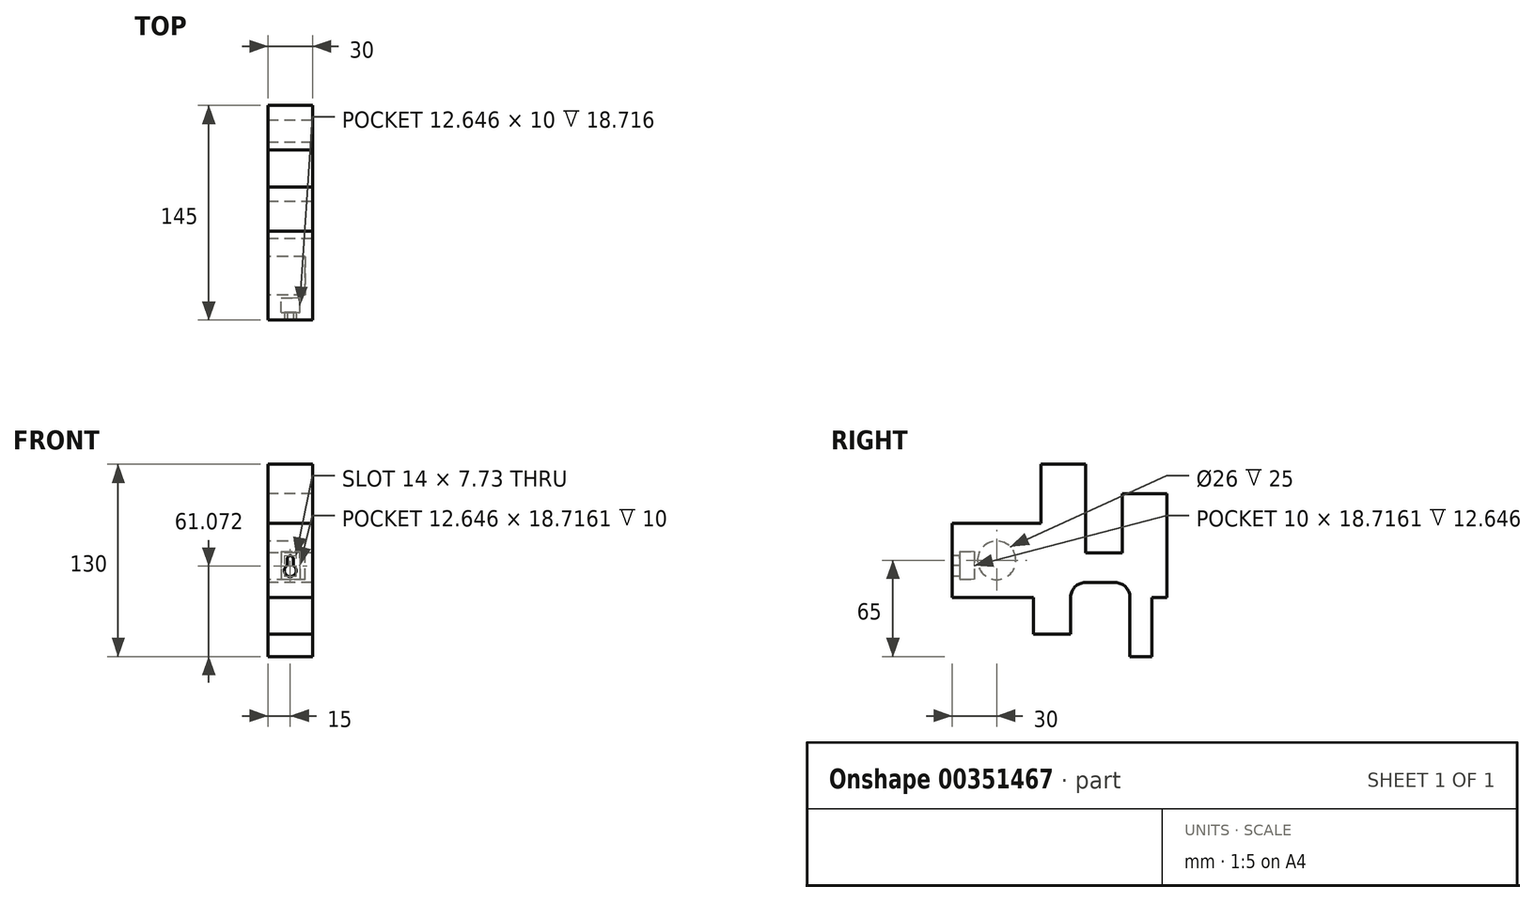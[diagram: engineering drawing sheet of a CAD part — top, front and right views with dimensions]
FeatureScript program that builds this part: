
annotation { "Feature Type Name" : "Feature", "Feature Type Description" : "" }
export const myFeature = defineFeature(function(context is Context, id is Id, definition is map)
    precondition{}
    {
        {
            var Q0;
            Q0=qCreatedBy(makeId("Right.planeOp"),FACE);
            var sketch = newSketch(context, id + "F0", { "sketchPlane" : qUnion([Q0])});
            skLineSegment(sketch, "E0", {"start": v(0, 0) * mm, "end": v(55, 0) * mm});
            skLineSegment(sketch, "E1", {"start": v(55, 0) * mm, "end": v(55, -25) * mm});
            skLineSegment(sketch, "E2", {"start": v(55, -25) * mm, "end": v(80, -25) * mm});
            skLineSegment(sketch, "E3", {"start": v(80, -25) * mm, "end": v(80, 0) * mm});
            skLineSegment(sketch, "E4", {"start": v(90, 10) * mm, "end": v(110, 10) * mm});
            skLineSegment(sketch, "E5", {"start": v(120, 0) * mm, "end": v(120, -40) * mm});
            skLineSegment(sketch, "E6", {"start": v(120, -40) * mm, "end": v(135, -40) * mm});
            skLineSegment(sketch, "E7", {"start": v(135, -40) * mm, "end": v(135, 0) * mm});
            skLineSegment(sketch, "E8", {"start": v(135, 0) * mm, "end": v(145, 0) * mm});
            skLineSegment(sketch, "E9", {"start": v(145, 0) * mm, "end": v(145, 70) * mm});
            skLineSegment(sketch, "E10", {"start": v(145, 70) * mm, "end": v(115, 70) * mm});
            skLineSegment(sketch, "E11", {"start": v(115, 70) * mm, "end": v(115, 30) * mm});
            skLineSegment(sketch, "E12", {"start": v(115, 30) * mm, "end": v(90, 30) * mm});
            skLineSegment(sketch, "E13", {"start": v(90, 30) * mm, "end": v(90, 90) * mm});
            skLineSegment(sketch, "E14", {"start": v(90, 90) * mm, "end": v(60, 90) * mm});
            skLineSegment(sketch, "E15", {"start": v(60, 90) * mm, "end": v(60, 50) * mm});
            skLineSegment(sketch, "E16", {"start": v(60, 50) * mm, "end": v(0, 50) * mm});
            skLineSegment(sketch, "E17", {"start": v(0, 50) * mm, "end": v(0, 0) * mm});
            skPoint(sketch, "E18.visualSharp", {"position": v(80, 10) * mm});
            skArc(sketch, "E18.filletArc", {"start": v(90, 10) * mm, "mid": v(82.93, 7.07) * mm, "end": v(80, 0) * mm});
            skPoint(sketch, "E19.visualSharp", {"position": v(120, 10) * mm});
            skArc(sketch, "E19.filletArc", {"start": v(120, 0) * mm, "mid": v(117.07, 7.07) * mm, "end": v(110, 10) * mm});
            skCircle(sketch, "E20", {"center": v(30, 25) * mm, "radius": 13 * mm});
            skSolve(sketch);
        }
        {
            var Q0;
            Q0=makeQuery(id+"F0.imprint","IMPRINT",FACE,{"disambiguationData":[TD([[makeQuery(id+"F0.imprint","IMPRINT",EDGE,{"derivedFrom":sQuery(id+"F0.wireOp",EDGE,"E0")}),1.0]])]});
            extrude(context, id + "F1", {"entities" : qUnion([Q0]), "depth" : 30 * mm});
        }
        {
            var Q0;
            Q0=makeQuery(id+"F1.opExtrude","CAP_FACE",FACE,{"disambiguationData":[OSD([sQuery(id+"F0.wireOp",EDGE,"E0"),sQuery(id+"F0.wireOp",EDGE,"E1"),sQuery(id+"F0.wireOp",EDGE,"E2"),sQuery(id+"F0.wireOp",EDGE,"E3"),sQuery(id+"F0.wireOp",EDGE,"E4"),sQuery(id+"F0.wireOp",EDGE,"E5"),sQuery(id+"F0.wireOp",EDGE,"E6"),sQuery(id+"F0.wireOp",EDGE,"E7"),sQuery(id+"F0.wireOp",EDGE,"E8"),sQuery(id+"F0.wireOp",EDGE,"E9"),sQuery(id+"F0.wireOp",EDGE,"E10"),sQuery(id+"F0.wireOp",EDGE,"E11"),sQuery(id+"F0.wireOp",EDGE,"E12"),sQuery(id+"F0.wireOp",EDGE,"E13"),sQuery(id+"F0.wireOp",EDGE,"E14"),sQuery(id+"F0.wireOp",EDGE,"E15"),sQuery(id+"F0.wireOp",EDGE,"E16"),sQuery(id+"F0.wireOp",EDGE,"E17"),sQuery(id+"F0.wireOp",EDGE,"E18.filletArc"),sQuery(id+"F0.wireOp",EDGE,"E19.filletArc"),sQuery(id+"F0.wireOp",EDGE,"E20")])],"isStart":false});
            var sketch = newSketch(context, id + "F2", { "sketchPlane" : qUnion([Q0])});
            skLineSegment(sketch, "E21.bottom", {"start": v(0, 50) * mm, "end": v(55, 50) * mm});
            skLineSegment(sketch, "E21.top", {"start": v(0, 0) * mm, "end": v(55, 0) * mm});
            skLineSegment(sketch, "E21.left", {"start": v(0, 50) * mm, "end": v(0, 0) * mm});
            skLineSegment(sketch, "E21.right", {"start": v(55, 50) * mm, "end": v(55, 0) * mm});
            skSolve(sketch);
        }
        {
            var Q0;
            Q0 = qSketchRegion(id + "F2", true);
            extrude(context, id + "F3", {"entities" : qUnion([Q0]), "operationType" : NewBodyOperationType.ADD, "oppositeDirection" : true, "depth" : 5 * mm});
        }
        {
            var Q0;
            Q0=makeQuery(id+"F1.opExtrude","SWEPT_FACE",FACE,{"disambiguationData":[OSD([sQuery(id+"F0.wireOp",EDGE,"E17")])]});
            var sketch = newSketch(context, id + "F4", { "sketchPlane" : qUnion([Q0])});
            skPoint(sketch, "E22.centerSnap0", {"position": v(15, 50) * mm});
            skPoint(sketch, "E22.centerSnap1", {"position": v(0, 25) * mm});
            skLineSegment(sketch, "E23.top", {"start": v(15, 15) * mm, "end": v(15, 15) * mm});
            skPoint(sketch, "E24.visualSharp", {"position": v(13, 15) * mm});
            skPoint(sketch, "E25.visualSharp", {"position": v(17, 15) * mm});
            skLineSegment(sketch, "E26.MirrorCS", {"start": v(13, 21.54) * mm, "end": v(13, 26.07) * mm});
            skLineSegment(sketch, "E27.MirrorCS", {"start": v(17, 21.54) * mm, "end": v(17, 26.07) * mm});
            skArc(sketch, "E28.MirrorCS", {"start": v(15, 28.07) * mm, "mid": v(16.41, 27.49) * mm, "end": v(17, 26.07) * mm});
            skArc(sketch, "E29.MirrorCS", {"start": v(13, 26.07) * mm, "mid": v(13.59, 27.49) * mm, "end": v(15, 28.07) * mm});
            skArc(sketch, "E30.MirrorCS", {"start": v(17, 21.54) * mm, "mid": v(15, 14.07) * mm, "end": v(13, 21.54) * mm});
            skPoint(sketch, "E22.center.orphan", {"position": v(15, 25) * mm});
            skSolve(sketch);
        }
        {
            var Q0;
            Q0=makeQuery(id+"F4.imprint","IMPRINT",FACE,{"disambiguationData":[TD([[makeQuery(id+"F4.imprint","IMPRINT",EDGE,{"derivedFrom":sQuery(id+"F4.wireOp",EDGE,"E26.MirrorCS")}),-1.0]])]});
            extrude(context, id + "F5", {"entities" : qUnion([Q0]), "operationType" : NewBodyOperationType.REMOVE, "oppositeDirection" : true, "depth" : 15 * mm});
        }
        {
            var Q0;
            Q0=makeQuery(id+"F5.boolean.opBoolean","COPY",FACE,{"derivedFrom":makeQuery(id+"F5.opExtrude","CAP_FACE",FACE,{"disambiguationData":[OSD([sQuery(id+"F4.wireOp",EDGE,"E26.MirrorCS"),sQuery(id+"F4.wireOp",EDGE,"E27.MirrorCS"),sQuery(id+"F4.wireOp",EDGE,"E28.MirrorCS"),sQuery(id+"F4.wireOp",EDGE,"E29.MirrorCS"),sQuery(id+"F4.wireOp",EDGE,"E30.MirrorCS")])],"isStart":false})});
            var sketch = newSketch(context, id + "F6", { "sketchPlane" : qUnion([Q0])});
            skLineSegment(sketch, "E31.bottom", {"start": v(8.85, 30.9) * mm, "end": v(21.5, 30.9) * mm});
            skLineSegment(sketch, "E31.top", {"start": v(8.85, 12.18) * mm, "end": v(21.5, 12.18) * mm});
            skLineSegment(sketch, "E31.left", {"start": v(8.85, 30.9) * mm, "end": v(8.85, 12.18) * mm});
            skLineSegment(sketch, "E31.right", {"start": v(21.5, 30.9) * mm, "end": v(21.5, 12.18) * mm});
            skSolve(sketch);
        }
        {
            var Q0;
            Q0 = qSketchRegion(id + "F6", true);
            extrude(context, id + "F7", {"entities" : qUnion([Q0]), "operationType" : NewBodyOperationType.REMOVE, "depth" : 10 * mm});
        }
    });
